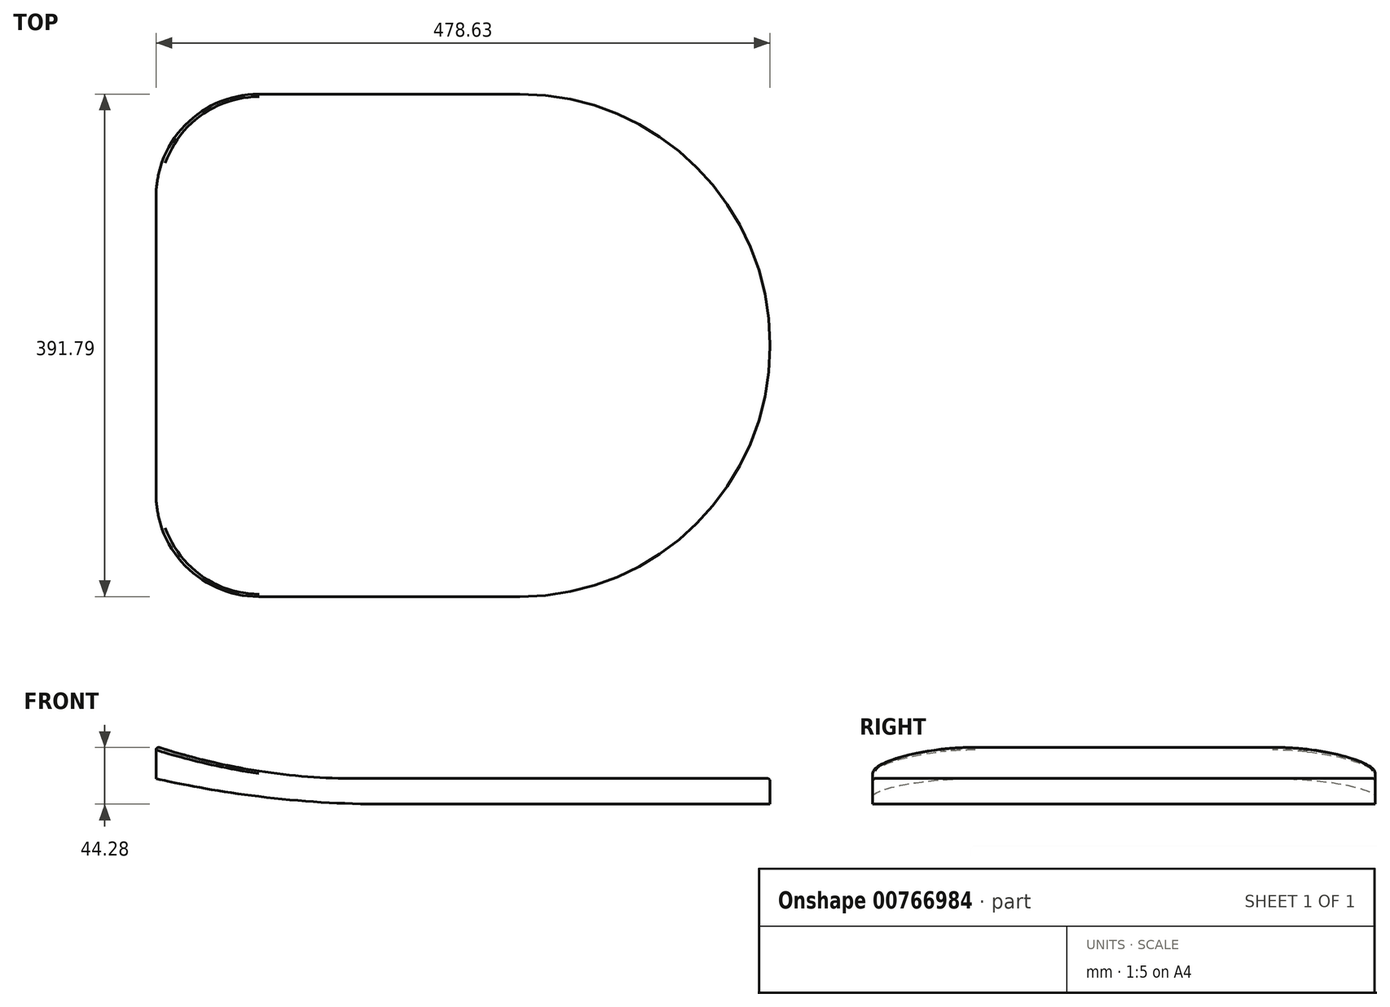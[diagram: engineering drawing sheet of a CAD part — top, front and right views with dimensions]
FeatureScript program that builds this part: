
annotation { "Feature Type Name" : "Feature", "Feature Type Description" : "" }
export const myFeature = defineFeature(function(context is Context, id is Id, definition is map)
    precondition{}
    {
        {
            var Q0;
            Q0=qCreatedBy(makeId("Top.planeOp"),FACE);
            var sketch = newSketch(context, id + "F0", { "sketchPlane" : qUnion([Q0])});
            skLineSegment(sketch, "E0.bottom", {"start": v(0, 0) * mm, "end": v(478.63, 0) * mm});
            skLineSegment(sketch, "E0.top", {"start": v(0, -391.79) * mm, "end": v(478.63, -391.79) * mm});
            skLineSegment(sketch, "E0.left", {"start": v(0, 0) * mm, "end": v(0, -391.79) * mm});
            skLineSegment(sketch, "E0.right", {"start": v(478.63, 0) * mm, "end": v(478.63, -391.79) * mm});
            skSolve(sketch);
        }
        {
            var Q0;
            Q0 = qSketchRegion(id + "F0", true);
            extrude(context, id + "F1", {"entities" : qUnion([Q0]), "depth" : 20 * mm, "offsetDistance" : 25 * mm});
        }
        {
            var Q0;
            Q0=makeQuery(id+"F1.opExtrude","CAP_FACE",FACE,{"disambiguationData":[OSD([sQuery(id+"F0.wireOp",EDGE,"E0.bottom"),sQuery(id+"F0.wireOp",EDGE,"E0.top"),sQuery(id+"F0.wireOp",EDGE,"E0.left"),sQuery(id+"F0.wireOp",EDGE,"E0.right")])],"isStart":false});
            var sketch = newSketch(context, id + "F2", { "sketchPlane" : qUnion([Q0])});
            skLineSegment(sketch, "E1.bottom", {"start": v(80, 0) * mm, "end": v(0, 0) * mm});
            skLineSegment(sketch, "E1.top", {"start": v(80, -391.79) * mm, "end": v(0, -391.79) * mm});
            skLineSegment(sketch, "E1.left", {"start": v(80, 0) * mm, "end": v(80, -391.79) * mm});
            skLineSegment(sketch, "E1.right", {"start": v(0, 0) * mm, "end": v(0, -391.79) * mm});
            skSolve(sketch);
        }
        {
            var Q0;
            Q0 = qSketchRegion(id + "F2", true);
            extrude(context, id + "F3", {"entities" : qUnion([Q0]), "operationType" : NewBodyOperationType.ADD, "depth" : 25 * mm, "offsetDistance" : 25 * mm});
        }
        {
            var Q0;
            Q0=makeQuery(id+"F3.opExtrude","CAP_EDGE",EDGE,{"disambiguationData":[OSD([sQuery(id+"F2.wireOp",EDGE,"E1.left")])],"isStart":false});
            chamfer(context, id + "F4", {"entities" : qUnion([Q0]), "chamferType" : ChamferType.TWO_OFFSETS, "width1" : 25 * mm, "oppositeDirection" : false, "width2" : 80 * mm, "tangentPropagation" : true});
        }
        {
            var Q0;
            Q0=makeQuery(id+"F4.opChamfer","BLEND_EDGE",EDGE,{"blendedFrom":[makeQuery(id+"F3.opExtrude","CAP_EDGE",EDGE,{"disambiguationData":[OSD([sQuery(id+"F2.wireOp",EDGE,"E1.left")])],"isStart":false}),makeQuery(id+"F1.opExtrude","CAP_FACE",FACE,{"disambiguationData":[OSD([sQuery(id+"F0.wireOp",EDGE,"E0.bottom"),sQuery(id+"F0.wireOp",EDGE,"E0.top"),sQuery(id+"F0.wireOp",EDGE,"E0.left"),sQuery(id+"F0.wireOp",EDGE,"E0.right")])],"isStart":false})],"blendedInto":[makeQuery(id+"F1.opExtrude","CAP_FACE",FACE,{"disambiguationData":[OSD([sQuery(id+"F0.wireOp",EDGE,"E0.bottom"),sQuery(id+"F0.wireOp",EDGE,"E0.top"),sQuery(id+"F0.wireOp",EDGE,"E0.left"),sQuery(id+"F0.wireOp",EDGE,"E0.right")])],"isStart":false})]});
            fillet(context, id + "F5", {"entities" : qUnion([Q0]), "radius" : 500 * mm, "tangentPropagation" : true, "allowEdgeOverflow" : false});
        }
        {
            var Q0;
            Q0=makeQuery(id+"F1.opExtrude","SWEPT_EDGE",EDGE,{"disambiguationData":[OSD([sQuery(id+"F0.wireOp",EDGE,"E0.top"),sQuery(id+"F0.wireOp",EDGE,"E0.right")])]});
            var Q1;
            Q1=makeQuery(id+"F1.opExtrude","SWEPT_EDGE",EDGE,{"disambiguationData":[OSD([sQuery(id+"F0.wireOp",EDGE,"E0.bottom"),sQuery(id+"F0.wireOp",EDGE,"E0.right")])]});
            fillet(context, id + "F6", {"entities" : qUnion([Q0, Q1]), "radius" : 195 * mm, "tangentPropagation" : true, "allowEdgeOverflow" : false});
        }
        {
            var Q0;
            Q0=makeQuery(id+"F1.opExtrude","CAP_EDGE",EDGE,{"disambiguationData":[OSD([sQuery(id+"F0.wireOp",EDGE,"E0.left")])],"isStart":true});
            chamfer(context, id + "F7", {"entities" : qUnion([Q0]), "chamferType" : ChamferType.TWO_OFFSETS, "width1" : 20 * mm, "oppositeDirection" : false, "width2" : 80 * mm, "tangentPropagation" : true});
        }
        {
            var Q0;
            {var subQ0=sQuery(id+"F0.wireOp",EDGE,"E0.left");Q0=makeQuery(id+"F7.opChamfer","BLEND_EDGE",EDGE,{"blendedFrom":[makeQuery(id+"F1.opExtrude","CAP_EDGE",EDGE,{"disambiguationData":[OSD([subQ0])],"isStart":true}),makeQuery(id+"F1.opExtrude","CAP_FACE",FACE,{"disambiguationData":[OSD([sQuery(id+"F0.wireOp",EDGE,"E0.bottom"),sQuery(id+"F0.wireOp",EDGE,"E0.top"),subQ0,sQuery(id+"F0.wireOp",EDGE,"E0.right")])],"isStart":true})],"blendedInto":[makeQuery(id+"F1.opExtrude","CAP_FACE",FACE,{"disambiguationData":[OSD([sQuery(id+"F0.wireOp",EDGE,"E0.bottom"),sQuery(id+"F0.wireOp",EDGE,"E0.top"),subQ0,sQuery(id+"F0.wireOp",EDGE,"E0.right")])],"isStart":true})]});}
            fillet(context, id + "F8", {"entities" : qUnion([Q0]), "radius" : 800 * mm, "tangentPropagation" : true, "allowEdgeOverflow" : false});
        }
        {
            var Q0;
            Q0=makeQuery(id+"F3.boolean.opBoolean","MERGE",EDGE,{"derivedFrom":[makeQuery(id+"F1.opExtrude","SWEPT_EDGE",EDGE,{"disambiguationData":[OSD([sQuery(id+"F0.wireOp",EDGE,"E0.bottom"),sQuery(id+"F0.wireOp",EDGE,"E0.left")])]}),makeQuery(id+"F3.opExtrude","SWEPT_EDGE",EDGE,{"disambiguationData":[OSD([sQuery(id+"F2.wireOp",EDGE,"E1.bottom"),sQuery(id+"F2.wireOp",EDGE,"E1.right")])]})]});
            var Q1;
            Q1=makeQuery(id+"F3.boolean.opBoolean","MERGE",EDGE,{"derivedFrom":[makeQuery(id+"F1.opExtrude","SWEPT_EDGE",EDGE,{"disambiguationData":[OSD([sQuery(id+"F0.wireOp",EDGE,"E0.top"),sQuery(id+"F0.wireOp",EDGE,"E0.left")])]}),makeQuery(id+"F3.opExtrude","SWEPT_EDGE",EDGE,{"disambiguationData":[OSD([sQuery(id+"F2.wireOp",EDGE,"E1.top"),sQuery(id+"F2.wireOp",EDGE,"E1.right")])]})]});
            fillet(context, id + "F9", {"entities" : qUnion([Q0, Q1]), "radius" : 80 * mm, "tangentPropagation" : true, "allowEdgeOverflow" : false});
        }
        {
            var Q0;
            Q0=makeQuery(id+"F1.opExtrude","CAP_EDGE",EDGE,{"disambiguationData":[OSD([sQuery(id+"F0.wireOp",EDGE,"E0.bottom")])],"isStart":false});
            var Q1;
            {var subQ0=sQuery(id+"F0.wireOp",EDGE,"E0.left");var subQ1=sQuery(id+"F0.wireOp",EDGE,"E0.bottom");Q1=makeQuery(id+"F9.opFillet","BLEND_EDGE",EDGE,{"blendedFrom":[makeQuery(id+"F3.boolean.opBoolean","MERGE",EDGE,{"derivedFrom":[makeQuery(id+"F1.opExtrude","SWEPT_EDGE",EDGE,{"disambiguationData":[OSD([subQ1,subQ0])]}),makeQuery(id+"F3.opExtrude","SWEPT_EDGE",EDGE,{"disambiguationData":[OSD([sQuery(id+"F2.wireOp",EDGE,"E1.bottom"),sQuery(id+"F2.wireOp",EDGE,"E1.right")])]})]}),makeQuery(id+"F5.opFillet","BLEND_FACE",FACE,{"disambiguationData":[OSD([subQ1,sQuery(id+"F0.wireOp",EDGE,"E0.top"),subQ0,sQuery(id+"F0.wireOp",EDGE,"E0.right"),sQuery(id+"F2.wireOp",EDGE,"E1.left")])]})],"blendedInto":[makeQuery(id+"F5.opFillet","BLEND_FACE",FACE,{"disambiguationData":[OSD([subQ1,sQuery(id+"F0.wireOp",EDGE,"E0.top"),subQ0,sQuery(id+"F0.wireOp",EDGE,"E0.right"),sQuery(id+"F2.wireOp",EDGE,"E1.left")])]})]});}
            var Q2;
            {var subQ0=sQuery(id+"F0.wireOp",EDGE,"E0.bottom");Q2=makeQuery(id+"F5.opFillet","BLEND_EDGE",EDGE,{"blendedFrom":[makeQuery(id+"F4.opChamfer","BLEND_EDGE",EDGE,{"blendedFrom":[makeQuery(id+"F3.opExtrude","CAP_EDGE",EDGE,{"disambiguationData":[OSD([sQuery(id+"F2.wireOp",EDGE,"E1.left")])],"isStart":false}),makeQuery(id+"F1.opExtrude","CAP_FACE",FACE,{"disambiguationData":[OSD([subQ0,sQuery(id+"F0.wireOp",EDGE,"E0.top"),sQuery(id+"F0.wireOp",EDGE,"E0.left"),sQuery(id+"F0.wireOp",EDGE,"E0.right")])],"isStart":false})],"blendedInto":[makeQuery(id+"F1.opExtrude","CAP_FACE",FACE,{"disambiguationData":[OSD([subQ0,sQuery(id+"F0.wireOp",EDGE,"E0.top"),sQuery(id+"F0.wireOp",EDGE,"E0.left"),sQuery(id+"F0.wireOp",EDGE,"E0.right")])],"isStart":false})]}),makeQuery(id+"F3.boolean.opBoolean","MERGE",FACE,{"derivedFrom":[makeQuery(id+"F1.opExtrude","SWEPT_FACE",FACE,{"disambiguationData":[OSD([subQ0])]}),makeQuery(id+"F3.opExtrude","SWEPT_FACE",FACE,{"disambiguationData":[OSD([sQuery(id+"F2.wireOp",EDGE,"E1.bottom")])]})]})],"blendedInto":[makeQuery(id+"F3.boolean.opBoolean","MERGE",FACE,{"derivedFrom":[makeQuery(id+"F1.opExtrude","SWEPT_FACE",FACE,{"disambiguationData":[OSD([subQ0])]}),makeQuery(id+"F3.opExtrude","SWEPT_FACE",FACE,{"disambiguationData":[OSD([sQuery(id+"F2.wireOp",EDGE,"E1.bottom")])]})]})]});}
            var Q3;
            {var subQ0=sQuery(id+"F0.wireOp",EDGE,"E0.right");var subQ1=sQuery(id+"F0.wireOp",EDGE,"E0.bottom");Q3=makeQuery(id+"F6.opFillet","BLEND_EDGE",EDGE,{"blendedFrom":[makeQuery(id+"F1.opExtrude","SWEPT_EDGE",EDGE,{"disambiguationData":[OSD([subQ1,subQ0])]}),makeQuery(id+"F1.opExtrude","CAP_FACE",FACE,{"disambiguationData":[OSD([subQ1,sQuery(id+"F0.wireOp",EDGE,"E0.top"),sQuery(id+"F0.wireOp",EDGE,"E0.left"),subQ0])],"isStart":false})],"blendedInto":[makeQuery(id+"F1.opExtrude","CAP_FACE",FACE,{"disambiguationData":[OSD([subQ1,sQuery(id+"F0.wireOp",EDGE,"E0.top"),sQuery(id+"F0.wireOp",EDGE,"E0.left"),subQ0])],"isStart":false})]});}
            var Q4;
            Q4=makeQuery(id+"F1.opExtrude","CAP_EDGE",EDGE,{"disambiguationData":[OSD([sQuery(id+"F0.wireOp",EDGE,"E0.right")])],"isStart":false});
            var Q5;
            {var subQ0=sQuery(id+"F0.wireOp",EDGE,"E0.right");var subQ1=sQuery(id+"F0.wireOp",EDGE,"E0.top");Q5=makeQuery(id+"F6.opFillet","BLEND_EDGE",EDGE,{"blendedFrom":[makeQuery(id+"F1.opExtrude","SWEPT_EDGE",EDGE,{"disambiguationData":[OSD([subQ1,subQ0])]}),makeQuery(id+"F1.opExtrude","CAP_FACE",FACE,{"disambiguationData":[OSD([sQuery(id+"F0.wireOp",EDGE,"E0.bottom"),subQ1,sQuery(id+"F0.wireOp",EDGE,"E0.left"),subQ0])],"isStart":false})],"blendedInto":[makeQuery(id+"F1.opExtrude","CAP_FACE",FACE,{"disambiguationData":[OSD([sQuery(id+"F0.wireOp",EDGE,"E0.bottom"),subQ1,sQuery(id+"F0.wireOp",EDGE,"E0.left"),subQ0])],"isStart":false})]});}
            var Q6;
            Q6=makeQuery(id+"F1.opExtrude","CAP_EDGE",EDGE,{"disambiguationData":[OSD([sQuery(id+"F0.wireOp",EDGE,"E0.top")])],"isStart":false});
            var Q7;
            {var subQ0=sQuery(id+"F0.wireOp",EDGE,"E0.top");Q7=makeQuery(id+"F5.opFillet","BLEND_EDGE",EDGE,{"blendedFrom":[makeQuery(id+"F4.opChamfer","BLEND_EDGE",EDGE,{"blendedFrom":[makeQuery(id+"F3.opExtrude","CAP_EDGE",EDGE,{"disambiguationData":[OSD([sQuery(id+"F2.wireOp",EDGE,"E1.left")])],"isStart":false}),makeQuery(id+"F1.opExtrude","CAP_FACE",FACE,{"disambiguationData":[OSD([sQuery(id+"F0.wireOp",EDGE,"E0.bottom"),subQ0,sQuery(id+"F0.wireOp",EDGE,"E0.left"),sQuery(id+"F0.wireOp",EDGE,"E0.right")])],"isStart":false})],"blendedInto":[makeQuery(id+"F1.opExtrude","CAP_FACE",FACE,{"disambiguationData":[OSD([sQuery(id+"F0.wireOp",EDGE,"E0.bottom"),subQ0,sQuery(id+"F0.wireOp",EDGE,"E0.left"),sQuery(id+"F0.wireOp",EDGE,"E0.right")])],"isStart":false})]}),makeQuery(id+"F3.boolean.opBoolean","MERGE",FACE,{"derivedFrom":[makeQuery(id+"F1.opExtrude","SWEPT_FACE",FACE,{"disambiguationData":[OSD([subQ0])]}),makeQuery(id+"F3.opExtrude","SWEPT_FACE",FACE,{"disambiguationData":[OSD([sQuery(id+"F2.wireOp",EDGE,"E1.top")])]})]})],"blendedInto":[makeQuery(id+"F3.boolean.opBoolean","MERGE",FACE,{"derivedFrom":[makeQuery(id+"F1.opExtrude","SWEPT_FACE",FACE,{"disambiguationData":[OSD([subQ0])]}),makeQuery(id+"F3.opExtrude","SWEPT_FACE",FACE,{"disambiguationData":[OSD([sQuery(id+"F2.wireOp",EDGE,"E1.top")])]})]})]});}
            var Q8;
            {var subQ0=sQuery(id+"F0.wireOp",EDGE,"E0.left");var subQ1=sQuery(id+"F0.wireOp",EDGE,"E0.top");Q8=makeQuery(id+"F9.opFillet","BLEND_EDGE",EDGE,{"blendedFrom":[makeQuery(id+"F3.boolean.opBoolean","MERGE",EDGE,{"derivedFrom":[makeQuery(id+"F1.opExtrude","SWEPT_EDGE",EDGE,{"disambiguationData":[OSD([subQ1,subQ0])]}),makeQuery(id+"F3.opExtrude","SWEPT_EDGE",EDGE,{"disambiguationData":[OSD([sQuery(id+"F2.wireOp",EDGE,"E1.top"),sQuery(id+"F2.wireOp",EDGE,"E1.right")])]})]}),makeQuery(id+"F5.opFillet","BLEND_FACE",FACE,{"disambiguationData":[OSD([sQuery(id+"F0.wireOp",EDGE,"E0.bottom"),subQ1,subQ0,sQuery(id+"F0.wireOp",EDGE,"E0.right"),sQuery(id+"F2.wireOp",EDGE,"E1.left")])]})],"blendedInto":[makeQuery(id+"F5.opFillet","BLEND_FACE",FACE,{"disambiguationData":[OSD([sQuery(id+"F0.wireOp",EDGE,"E0.bottom"),subQ1,subQ0,sQuery(id+"F0.wireOp",EDGE,"E0.right"),sQuery(id+"F2.wireOp",EDGE,"E1.left")])]})]});}
            fillet(context, id + "F10", {"entities" : qUnion([Q0, Q1, Q2, Q3, Q4, Q5, Q6, Q7, Q8]), "radius" : 2 * mm, "tangentPropagation" : true, "allowEdgeOverflow" : false});
        }
    });
